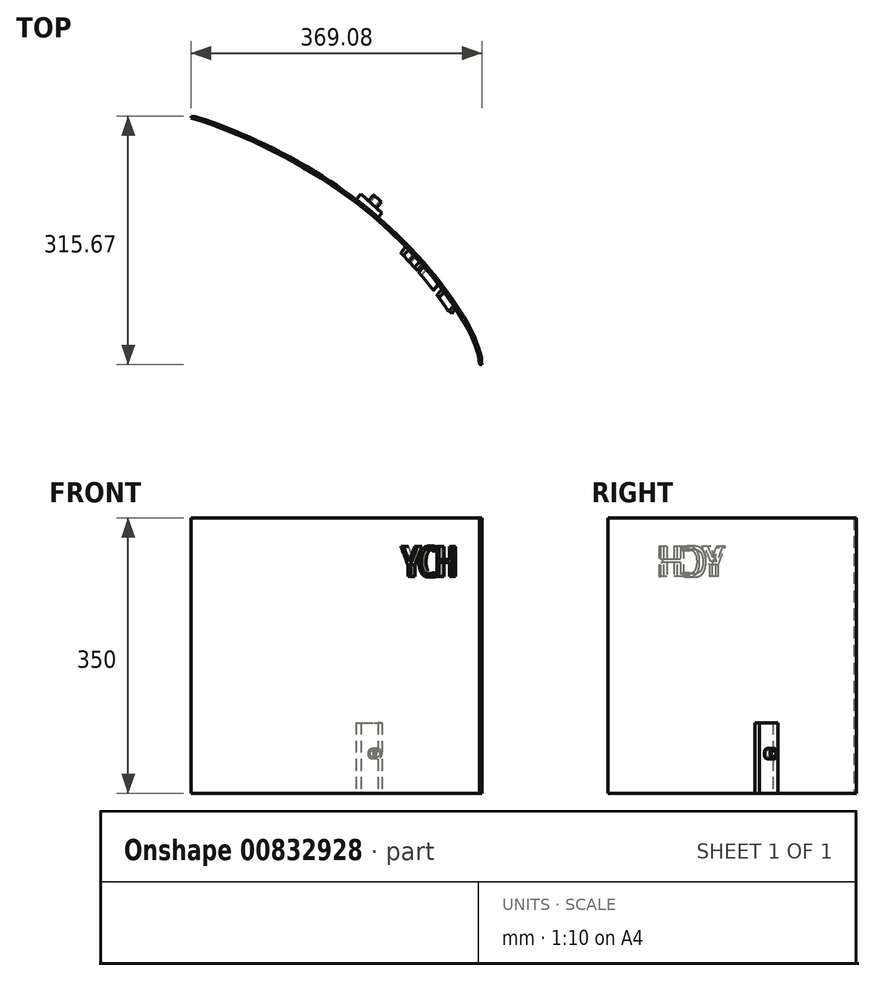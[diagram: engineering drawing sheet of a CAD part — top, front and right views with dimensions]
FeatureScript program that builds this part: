
annotation { "Feature Type Name" : "Feature", "Feature Type Description" : "" }
export const myFeature = defineFeature(function(context is Context, id is Id, definition is map)
    precondition{}
    {
        {
            var Q0;
            Q0=qCreatedBy(makeId("Top.planeOp"),FACE);
            var sketch = newSketch(context, id + "F0", { "sketchPlane" : qUnion([Q0])});
            skFitSpline(sketch, "E0", {"points": [v(-223.6, 116.45) * mm, v(-1.04, -0.95) * mm, v(142.46, -196.31) * mm], "startDerivative": vector(222.13, -55.27) * mm, "endDerivative": vector(0, -230.66) * mm});
            skFitSpline(sketch, "E1.0", {"points": [v(-222.88, 119.36) * mm, v(-218.15, 118.19) * mm, v(-206.78, 114.88) * mm, v(-184.75, 107.07) * mm, v(-158.68, 96.48) * mm, v(-129.51, 83.16) * mm, v(-98.22, 67.16) * mm, v(-65.76, 48.54) * mm, v(-38.54, 30.88) * mm, v(-17.14, 15.5) * mm, v(-1.4, 3.35) * mm, v(13.91, -9.43) * mm, v(33.63, -27.13) * mm, v(56.83, -50.23) * mm, v(81.84, -78.55) * mm, v(103.51, -106.53) * mm, v(121.33, -133.25) * mm, v(132.53, -153.7) * mm, v(139.06, -168.54) * mm, v(142.67, -178.8) * mm, v(144.92, -188.14) * mm, v(145.46, -193.7) * mm, v(145.46, -196.31) * mm]});
            skLineSegment(sketch, "E2", {"start": v(-223.6, 116.45) * mm, "end": v(-222.88, 119.36) * mm});
            skLineSegment(sketch, "E3", {"start": v(142.46, -196.31) * mm, "end": v(145.46, -196.31) * mm});
            skLineSegment(sketch, "E4", {"start": v(-14.3, 13.23) * mm, "end": v(-7.95, 20.02) * mm});
            skLineSegment(sketch, "E5", {"start": v(-7.95, 20.02) * mm, "end": v(18.68, -3.88) * mm});
            skLineSegment(sketch, "E6", {"start": v(18.68, -3.88) * mm, "end": v(13.72, -9.41) * mm});
            skLineSegment(sketch, "E7", {"start": v(122.46, -196.31) * mm, "end": v(117.46, -196.31) * mm});
            skLineSegment(sketch, "E8", {"start": v(-228.43, 97.04) * mm, "end": v(-229.64, 92.19) * mm});
            skFitSpline(sketch, "E9.0", {"points": [v(-226.01, 106.75) * mm, v(-223.86, 106.2) * mm, v(-218.98, 104.88) * mm, v(-207.28, 101.26) * mm, v(-189.4, 94.93) * mm, v(-163.84, 84.55) * mm, v(-135.18, 71.45) * mm, v(-104.42, 55.72) * mm, v(-77.85, 40.48) * mm, v(-56.52, 27.05) * mm, v(-40.6, 16.36) * mm, v(-24.9, 5.07) * mm, v(-12.1, -4.82) * mm, v(-2.07, -13.02) * mm, v(7.8, -21.42) * mm, v(19.85, -32.23) * mm, v(33.75, -45.6) * mm, v(51.44, -63.77) * mm, v(71.83, -86.85) * mm, v(92.98, -114.16) * mm, v(107.36, -135.75) * mm, v(116.65, -151.78) * mm, v(122.44, -163.04) * mm, v(126.98, -173.38) * mm, v(130.22, -182.6) * mm, v(131.78, -189.16) * mm, v(132.37, -193.57) * mm, v(132.46, -195.46) * mm, v(132.46, -196.31) * mm]});
            skLineSegment(sketch, "E10", {"start": v(132.46, -196.31) * mm, "end": v(122.46, -196.31) * mm});
            skLineSegment(sketch, "E11", {"start": v(-226.01, 106.75) * mm, "end": v(-228.43, 97.04) * mm});
            skFitSpline(sketch, "E12.0", {"points": [v(-233.26, 77.63) * mm, v(-232.41, 77.42) * mm, v(-230.53, 76.93) * mm, v(-226.1, 75.68) * mm, v(-219.5, 73.64) * mm, v(-210.12, 70.44) * mm, v(-195.95, 65.2) * mm, v(-175.56, 56.92) * mm, v(-147.96, 44.3) * mm, v(-123.25, 31.65) * mm, v(-102.98, 20.31) * mm, v(-87.66, 11.21) * mm, v(-72.34, 1.54) * mm, v(-59.68, -6.98) * mm, v(-49.69, -14.06) * mm, v(-42.27, -19.5) * mm, v(-34.95, -25.07) * mm, v(-27.75, -30.76) * mm, v(-20.67, -36.58) * mm, v(-13.67, -42.55) * mm, v(-6.77, -48.65) * mm, v(2.27, -56.93) * mm, v(13.25, -67.53) * mm, v(25.85, -80.51) * mm, v(37.78, -93.62) * mm, v(48.96, -106.73) * mm, v(59.31, -119.7) * mm, v(68.75, -132.36) * mm, v(77.2, -144.59) * mm, v(84.56, -156.2) * mm, v(89.73, -165.19) * mm, v(93.24, -171.87) * mm, v(95.55, -176.57) * mm, v(97.54, -180.95) * mm, v(99.18, -184.94) * mm, v(100.26, -187.9) * mm, v(100.96, -190) * mm, v(101.4, -191.43) * mm, v(101.75, -192.73) * mm, v(102.02, -193.86) * mm, v(102.2, -194.66) * mm, v(102.3, -195.19) * mm, v(102.35, -195.53) * mm, v(102.4, -195.83) * mm, v(102.42, -196.03) * mm, v(102.44, -196.16) * mm, v(102.44, -196.25) * mm, v(102.45, -196.32) * mm, v(102.46, -196.36) * mm, v(102.46, -196.39) * mm, v(102.46, -196.4) * mm, v(102.46, -196.42) * mm, v(102.46, -196.43) * mm, v(102.46, -196.43) * mm, v(102.46, -196.43) * mm, v(102.46, -196.44) * mm, v(102.46, -196.44) * mm, v(102.46, -196.44) * mm, v(102.46, -196.44) * mm, v(102.46, -196.44) * mm, v(102.46, -196.44) * mm, v(102.46, -196.45) * mm, v(102.46, -196.46) * mm, v(102.46, -196.48) * mm, v(102.46, -196.51) * mm, v(102.47, -196.55) * mm, v(102.47, -196.6) * mm, v(102.47, -196.65) * mm, v(102.47, -196.73) * mm, v(102.48, -196.84) * mm, v(102.49, -196.99) * mm, v(102.5, -197.17) * mm, v(102.5, -197.34) * mm, v(102.51, -197.58) * mm, v(102.53, -197.87) * mm, v(102.54, -198.1) * mm, v(102.54, -198.22) * mm]});
            skLineSegment(sketch, "E13", {"start": v(117.46, -196.31) * mm, "end": v(102.45, -196.31) * mm});
            skLineSegment(sketch, "E14", {"start": v(-229.64, 92.19) * mm, "end": v(-233.26, 77.63) * mm});
            skSolve(sketch);
        }
        {
            var Q0;
            Q0=makeQuery(id+"F0.imprint","IMPRINT",FACE,{"disambiguationData":[TD([[makeQuery(id+"F0.imprint","IMPRINT",EDGE,{"derivedFrom":sQuery(id+"F0.wireOp",EDGE,"E0")}),1.0]])]});
            extrude(context, id + "F1", {"entities" : qUnion([Q0]), "depth" : 350 * mm, "offsetDistance" : 25 * mm});
        }
        {
            var Q0;
            {var subQ0=sQuery(id+"F0.wireOp",EDGE,"E4");Q0=makeQuery(id+"F0.imprint","IMPRINT",FACE,{"disambiguationData":[TD([[makeQuery(id+"F0.imprint","IMPRINT",EDGE,{"derivedFrom":subQ0}),-1.0]])]});}
            extrude(context, id + "F2", {"entities" : qUnion([Q0]), "operationType" : NewBodyOperationType.ADD, "depth" : 90 * mm, "offsetDistance" : 25 * mm});
        }
        {
            var Q0;
            Q0=makeQuery(id+"F2.opExtrude","SWEPT_FACE",FACE,{"disambiguationData":[OSD([sQuery(id+"F0.wireOp",EDGE,"E5")])]});
            var sketch = newSketch(context, id + "F3", { "sketchPlane" : qUnion([Q0])});
            skCircle(sketch, "E15", {"center": v(0, 50.62) * mm, "radius": 6.86 * mm});
            skCircle(sketch, "E16", {"center": v(0, 50.62) * mm, "radius": 4 * mm});
            skSolve(sketch);
        }
        {
            var Q0;
            Q0=makeQuery(id+"F3.imprint","IMPRINT",FACE,{"disambiguationData":[TD([[makeQuery(id+"F3.imprint","IMPRINT",EDGE,{"derivedFrom":sQuery(id+"F3.wireOp",EDGE,"E15")}),1.0]])]});
            extrude(context, id + "F4", {"entities" : qUnion([Q0]), "operationType" : NewBodyOperationType.ADD, "depth" : 10 * mm, "offsetDistance" : 25 * mm});
        }
        {
            var Q0;
            Q0=qCreatedBy(makeId("Front.planeOp"),FACE);
            var sketch = newSketch(context, id + "F5", { "sketchPlane" : qUnion([Q0])});
            skLineSegment(sketch, "E17", {"start": v(0, 0) * mm, "end": v(0, 95.14) * mm});
            skSolve(sketch);
        }
        {
            var Q0;
            Q0=qCreatedBy(makeId("Right.planeOp"),FACE);
            var Q1;
            Q1=sQuery(id+"F5.wireOp",EDGE,"E17");
            cPlane(context, id + "F6", {"entities" : qUnion([Q0, Q1]), "cplaneType" : CPlaneType.LINE_ANGLE, "offset" : 25 * mm, "angle" : 53 * degree, "width" : 150 * mm, "height" : 150 * mm});
        }
        {
            var Q0;
            Q0=qCreatedBy(id+"F6.planeOp",FACE);
            cPlane(context, id + "F7", {"entities" : qUnion([Q0]), "cplaneType" : CPlaneType.OFFSET, "offset" : 40 * mm, "width" : 150 * mm, "height" : 150 * mm});
        }
        {
            var Q0;
            Q0=qCreatedBy(id+"F7.planeOp",FACE);
            var sketch = newSketch(context, id + "F8", { "sketchPlane" : qUnion([Q0])});
            skText(sketch, "E18", { "text": "YCH", "fontName": "OpenSans-Regular.ttf"});
            const initialGuessF8  = {"E18": [0.06703, 0.2755, 1, 0, 0.03853]};
            skSetInitialGuess(sketch, initialGuessF8);
            skSolve(sketch);
        }
        {
            var Q0;
            Q0 = qSketchRegion(id + "F8", true);
            extrude(context, id + "F9", {"entities" : qUnion([Q0]), "operationType" : NewBodyOperationType.ADD, "endBound" : BoundingType.UP_TO_NEXT, "oppositeDirection" : true, "depth" : 25 * mm, "offsetDistance" : 25 * mm});
        }
        {
            var Q0;
            Q0=makeQuery(id+"F0.imprint","IMPRINT",FACE,{"disambiguationData":[TD([[makeQuery(id+"F0.imprint","IMPRINT",EDGE,{"derivedFrom":sQuery(id+"F0.wireOp",EDGE,"E7")}),-1.0]])]});
            extrude(context, id + "F10", {"entities" : qUnion([Q0]), "operationType" : NewBodyOperationType.REMOVE, "endBound" : BoundingType.THROUGH_ALL, "depth" : 500 * mm, "offsetDistance" : 25 * mm});
        }
    });
